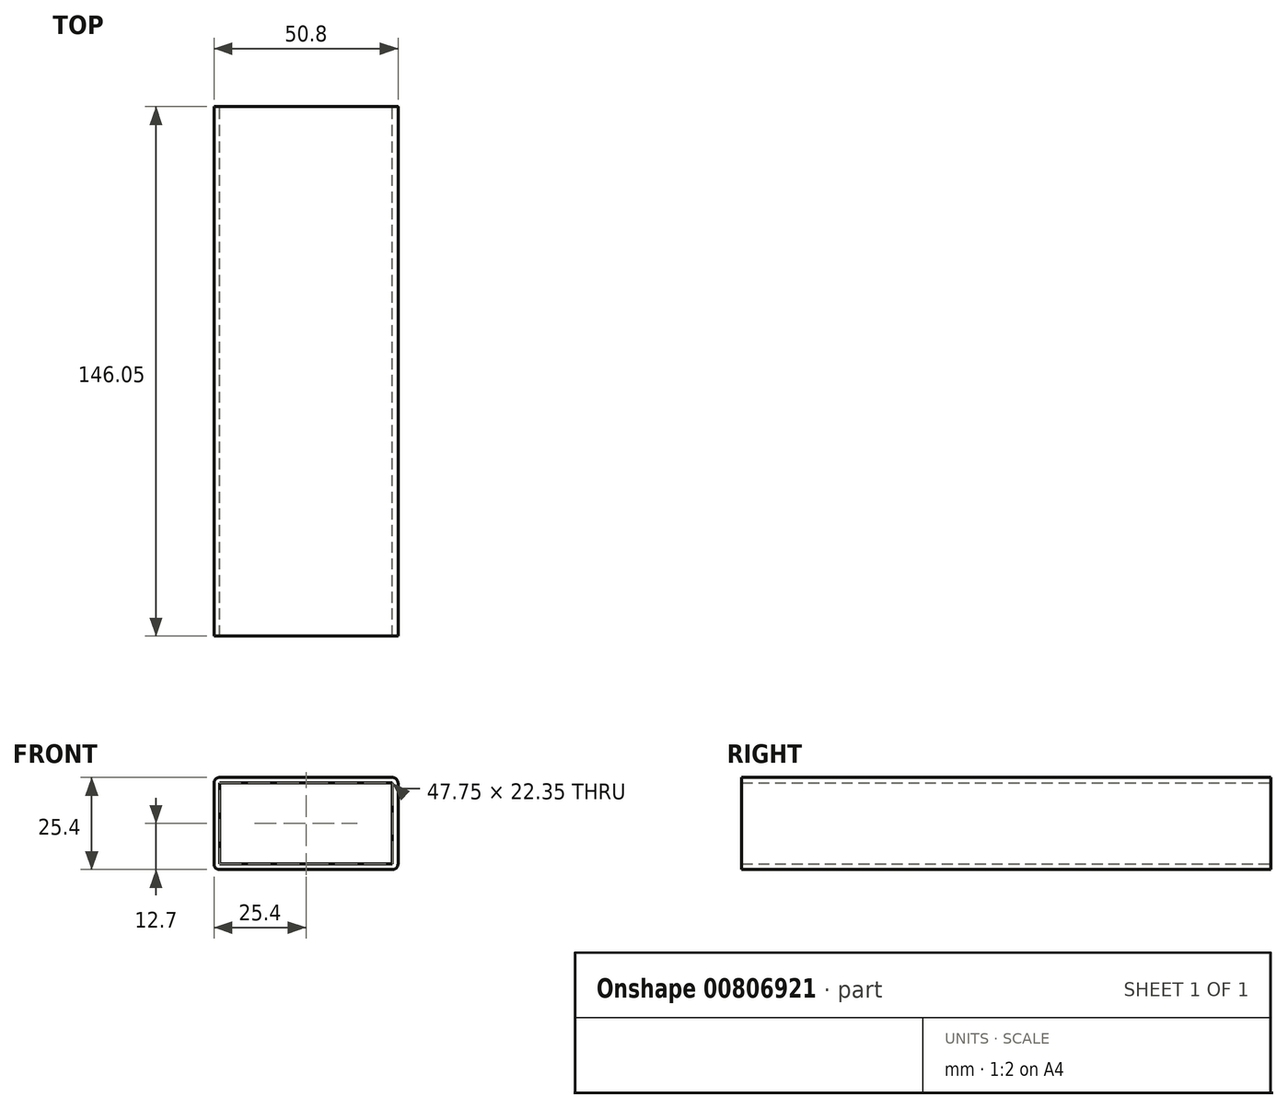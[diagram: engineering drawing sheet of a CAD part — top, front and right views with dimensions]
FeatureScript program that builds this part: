
annotation { "Feature Type Name" : "Feature", "Feature Type Description" : "" }
export const myFeature = defineFeature(function(context is Context, id is Id, definition is map)
    precondition{}
    {
        {
            var Q0;
            Q0=qCreatedBy(makeId("Front.planeOp"),FACE);
            var sketch = newSketch(context, id + "F0", { "sketchPlane" : qUnion([Q0])});
            skLineSegment(sketch, "E0.bottom", {"start": v(1.52, 0) * mm, "end": v(49.28, 0) * mm});
            skLineSegment(sketch, "E0.top", {"start": v(1.52, 25.4) * mm, "end": v(49.28, 25.4) * mm});
            skLineSegment(sketch, "E0.left", {"start": v(0, 1.52) * mm, "end": v(0, 23.88) * mm});
            skLineSegment(sketch, "E0.right", {"start": v(50.8, 1.52) * mm, "end": v(50.8, 23.88) * mm});
            skPoint(sketch, "E1.visualSharp", {"position": v(0, 25.4) * mm});
            skArc(sketch, "E1.filletArc", {"start": v(1.52, 25.4) * mm, "mid": v(0.45, 24.95) * mm, "end": v(0, 23.88) * mm});
            skPoint(sketch, "E2.visualSharp", {"position": v(50.8, 25.4) * mm});
            skArc(sketch, "E2.filletArc", {"start": v(50.8, 23.88) * mm, "mid": v(50.35, 24.95) * mm, "end": v(49.28, 25.4) * mm});
            skPoint(sketch, "E3.visualSharp", {"position": v(50.8, 0) * mm});
            skArc(sketch, "E3.filletArc", {"start": v(49.28, 0) * mm, "mid": v(50.35, 0.45) * mm, "end": v(50.8, 1.52) * mm});
            skPoint(sketch, "E4.visualSharp", {"position": v(0, 0) * mm});
            skArc(sketch, "E4.filletArc", {"start": v(0, 1.52) * mm, "mid": v(0.45, 0.45) * mm, "end": v(1.52, 0) * mm});
            skLineSegment(sketch, "E5.0", {"start": v(49.28, 1.52) * mm, "end": v(49.28, 23.88) * mm});
            skLineSegment(sketch, "E5.1", {"start": v(1.52, 1.52) * mm, "end": v(49.28, 1.52) * mm});
            skLineSegment(sketch, "E5.2", {"start": v(1.52, 1.52) * mm, "end": v(1.52, 23.88) * mm});
            skLineSegment(sketch, "E5.3", {"start": v(1.52, 23.88) * mm, "end": v(49.28, 23.88) * mm});
            skSolve(sketch);
        }
        {
            var Q0;
            Q0 = qSketchRegion(id + "F0", true);
            extrude(context, id + "F1", {"entities" : qUnion([Q0]), "depth" : 146.05 * mm, "offsetDistance" : 25.4 * mm});
        }
    });
